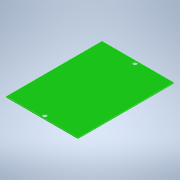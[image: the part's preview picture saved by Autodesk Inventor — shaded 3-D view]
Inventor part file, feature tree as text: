
AUTODESK INVENTOR PART (.ipt)
format: ipt  version: 2022 (Build 260153000, 153)  size: 3,027,968 bytes
history: native  units: in
note: dims shown in document units (in); Inventor stores cm internally (conversion verified against a paired STEP export)
features: extrude x2, hole x1, sketch x1
ambient origin geometry x8: Origin, YZ Plane, XZ Plane, XY Plane, X Axis, Y Axis, Z Axis, Center Point
bodies: Solid1 (feature_tree)
feature tree (4):
  extrude  "Extrusion1"  Depth=2.2638in
  hole  "Hole2"  [1 undecoded]
  extrude  "Extrusion4"  Depth=0.0039in
  sketch  "Sketch1"  dims[d0=1.6969in d1=2.2638in d2=0.0197in d3=0.0in d37=0.0866in d38=0.2726in d39=0.1732in d40=0.0787in d41=90.0deg d42=0.315in d43=0.8108in d57=0.0039in d58=0.0118in d59=0.128in d60=0.126in d61=27.9528in d63=0.0098in d64=0.3937in d66=0.3937in d68=0.0118in d69=0.0039in d70=0.0049in d71=0.003in d72=27.9528in d74=0.0098in d75=0.3937in d77=0.3937in d79=0.002in d80=0.0in d81=0.7874in d83=0.8504in d84=0.3937in d86=0.3937in d88=0.7874in d90=360.0deg d92=0.0689in d95=0.8484in d96=1.6969in d97=0.0689in]
note: 1 required parameter value undecoded (feature->parameter linkage not recoverable at this tier; creation-order binding heuristic only, values carry confidence <= 0.55)
